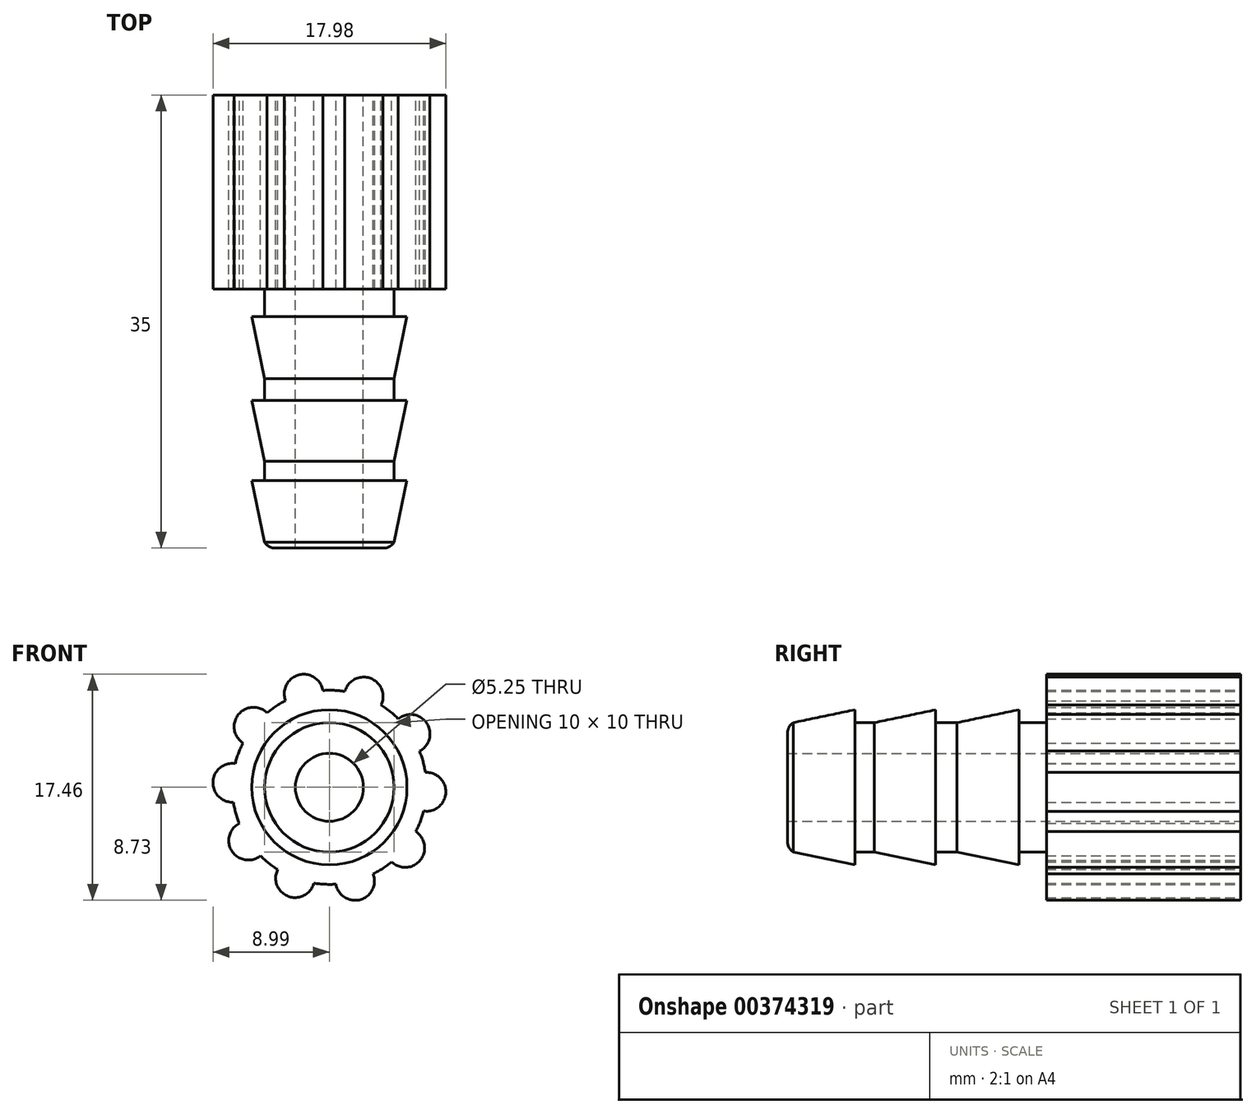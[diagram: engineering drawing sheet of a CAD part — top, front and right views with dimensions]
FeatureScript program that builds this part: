
annotation { "Feature Type Name" : "Feature", "Feature Type Description" : "" }
export const myFeature = defineFeature(function(context is Context, id is Id, definition is map)
    precondition{}
    {
        {
            var Q0;
            Q0=qCreatedBy(makeId("Front.planeOp"),FACE);
            var sketch = newSketch(context, id + "F0", { "sketchPlane" : qUnion([Q0])});
            skArc(sketch, "E0", {"start": v(-3.38, 6.7) * mm, "mid": v(-4.12, 6.27) * mm, "end": v(-4.8, 5.76) * mm});
            skArc(sketch, "E1", {"start": v(3.99, 6.35) * mm, "mid": v(3.18, 8.42) * mm, "end": v(1.2, 7.4) * mm});
            skArc(sketch, "E2.1.0", {"start": v(-0.5, 7.48) * mm, "mid": v(-2.38, 8.68) * mm, "end": v(-3.38, 6.7) * mm});
            skArc(sketch, "E2.2.0", {"start": v(-4.8, 5.76) * mm, "mid": v(-7.03, 5.62) * mm, "end": v(-6.67, 3.43) * mm});
            skArc(sketch, "E2.3.0", {"start": v(-7.27, 1.83) * mm, "mid": v(-9, 0.42) * mm, "end": v(-7.41, -1.15) * mm});
            skArc(sketch, "E2.4.0", {"start": v(-6.96, -2.8) * mm, "mid": v(-7.52, -4.95) * mm, "end": v(-5.32, -5.29) * mm});
            skArc(sketch, "E2.5.0", {"start": v(-3.99, -6.35) * mm, "mid": v(-3.18, -8.42) * mm, "end": v(-1.2, -7.4) * mm});
            skArc(sketch, "E2.6.0", {"start": v(0.5, -7.48) * mm, "mid": v(2.38, -8.68) * mm, "end": v(3.38, -6.7) * mm});
            skArc(sketch, "E2.7.0", {"start": v(4.8, -5.76) * mm, "mid": v(7.03, -5.62) * mm, "end": v(6.67, -3.43) * mm});
            skArc(sketch, "E2.8.0", {"start": v(7.27, -1.83) * mm, "mid": v(9, -0.42) * mm, "end": v(7.41, 1.15) * mm});
            skArc(sketch, "E2.9.0", {"start": v(6.96, 2.8) * mm, "mid": v(7.52, 4.95) * mm, "end": v(5.32, 5.29) * mm});
            skArc(sketch, "E3.trimOffspring", {"start": v(1.2, 7.4) * mm, "mid": v(0.35, 7.5) * mm, "end": v(-0.5, 7.48) * mm});
            skArc(sketch, "E4.trimOffspring", {"start": v(5.32, 5.29) * mm, "mid": v(4.69, 5.86) * mm, "end": v(3.99, 6.35) * mm});
            skArc(sketch, "E5.trimOffspring", {"start": v(7.41, 1.15) * mm, "mid": v(7.23, 1.98) * mm, "end": v(6.96, 2.8) * mm});
            skArc(sketch, "E6.trimOffspring", {"start": v(6.67, -3.43) * mm, "mid": v(7.02, -2.65) * mm, "end": v(7.27, -1.83) * mm});
            skArc(sketch, "E7.trimOffspring", {"start": v(3.38, -6.7) * mm, "mid": v(4.12, -6.27) * mm, "end": v(4.8, -5.76) * mm});
            skArc(sketch, "E8.trimOffspring", {"start": v(-1.2, -7.4) * mm, "mid": v(-0.35, -7.5) * mm, "end": v(0.5, -7.48) * mm});
            skArc(sketch, "E9.trimOffspring", {"start": v(-5.32, -5.29) * mm, "mid": v(-4.69, -5.86) * mm, "end": v(-3.99, -6.35) * mm});
            skArc(sketch, "E10.trimOffspring", {"start": v(-7.41, -1.15) * mm, "mid": v(-7.23, -1.98) * mm, "end": v(-6.96, -2.8) * mm});
            skArc(sketch, "E11.trimOffspring", {"start": v(-6.67, 3.43) * mm, "mid": v(-7.02, 2.65) * mm, "end": v(-7.27, 1.83) * mm});
            skSolve(sketch);
        }
        {
            var Q0;
            Q0=makeQuery(id+"F0.imprint","IMPRINT",FACE,{"disambiguationData":[TD([[makeQuery(id+"F0.imprint","IMPRINT",EDGE,{"derivedFrom":sQuery(id+"F0.wireOp",EDGE,"E0")}),1.0]])]});
            extrude(context, id + "F1", {"entities" : qUnion([Q0]), "depth" : 15 * mm});
        }
        {
            var Q0;
            Q0=makeQuery(id+"F1.opExtrude","CAP_FACE",FACE,{"disambiguationData":[OSD([sQuery(id+"F0.wireOp",EDGE,"E0"),sQuery(id+"F0.wireOp",EDGE,"E1"),sQuery(id+"F0.wireOp",EDGE,"E2.1.0"),sQuery(id+"F0.wireOp",EDGE,"E2.2.0"),sQuery(id+"F0.wireOp",EDGE,"E2.3.0"),sQuery(id+"F0.wireOp",EDGE,"E2.4.0"),sQuery(id+"F0.wireOp",EDGE,"E2.5.0"),sQuery(id+"F0.wireOp",EDGE,"E2.6.0"),sQuery(id+"F0.wireOp",EDGE,"E2.7.0"),sQuery(id+"F0.wireOp",EDGE,"E2.8.0"),sQuery(id+"F0.wireOp",EDGE,"E2.9.0"),sQuery(id+"F0.wireOp",EDGE,"E3.trimOffspring"),sQuery(id+"F0.wireOp",EDGE,"E4.trimOffspring"),sQuery(id+"F0.wireOp",EDGE,"E5.trimOffspring"),sQuery(id+"F0.wireOp",EDGE,"E6.trimOffspring"),sQuery(id+"F0.wireOp",EDGE,"E7.trimOffspring"),sQuery(id+"F0.wireOp",EDGE,"E8.trimOffspring"),sQuery(id+"F0.wireOp",EDGE,"E9.trimOffspring"),sQuery(id+"F0.wireOp",EDGE,"E10.trimOffspring"),sQuery(id+"F0.wireOp",EDGE,"E11.trimOffspring")])],"isStart":true});
            var sketch = newSketch(context, id + "F2", { "sketchPlane" : qUnion([Q0])});
            skCircle(sketch, "E12", {"center": v(0, 0) * mm, "radius": 2.63 * mm});
            skSolve(sketch);
        }
        {
            var Q0;
            Q0=makeQuery(id+"F2.imprint","IMPRINT",FACE,{"disambiguationData":[TD([[makeQuery(id+"F2.imprint","IMPRINT",EDGE,{"derivedFrom":sQuery(id+"F2.wireOp",EDGE,"E12")}),1.0]])]});
            extrude(context, id + "F3", {"entities" : qUnion([Q0]), "operationType" : NewBodyOperationType.REMOVE, "oppositeDirection" : true, "depth" : 12 * mm});
        }
        {
            var Q0;
            Q0=makeQuery(id+"F1.opExtrude","CAP_FACE",FACE,{"disambiguationData":[OSD([sQuery(id+"F0.wireOp",EDGE,"E0"),sQuery(id+"F0.wireOp",EDGE,"E1"),sQuery(id+"F0.wireOp",EDGE,"E2.1.0"),sQuery(id+"F0.wireOp",EDGE,"E2.2.0"),sQuery(id+"F0.wireOp",EDGE,"E2.3.0"),sQuery(id+"F0.wireOp",EDGE,"E2.4.0"),sQuery(id+"F0.wireOp",EDGE,"E2.5.0"),sQuery(id+"F0.wireOp",EDGE,"E2.6.0"),sQuery(id+"F0.wireOp",EDGE,"E2.7.0"),sQuery(id+"F0.wireOp",EDGE,"E2.8.0"),sQuery(id+"F0.wireOp",EDGE,"E2.9.0"),sQuery(id+"F0.wireOp",EDGE,"E3.trimOffspring"),sQuery(id+"F0.wireOp",EDGE,"E4.trimOffspring"),sQuery(id+"F0.wireOp",EDGE,"E5.trimOffspring"),sQuery(id+"F0.wireOp",EDGE,"E6.trimOffspring"),sQuery(id+"F0.wireOp",EDGE,"E7.trimOffspring"),sQuery(id+"F0.wireOp",EDGE,"E8.trimOffspring"),sQuery(id+"F0.wireOp",EDGE,"E9.trimOffspring"),sQuery(id+"F0.wireOp",EDGE,"E10.trimOffspring"),sQuery(id+"F0.wireOp",EDGE,"E11.trimOffspring")])],"isStart":false});
            var sketch = newSketch(context, id + "F4", { "sketchPlane" : qUnion([Q0])});
            skCircle(sketch, "E13", {"center": v(0, 0) * mm, "radius": 5 * mm});
            skSolve(sketch);
        }
        {
            var Q0;
            Q0 = qSketchRegion(id + "F4", true);
            extrude(context, id + "F5", {"entities" : qUnion([Q0]), "operationType" : NewBodyOperationType.ADD, "depth" : 20 * mm});
        }
        {
            var Q0;
            Q0=qCreatedBy(makeId("Right.planeOp"),FACE);
            var sketch = newSketch(context, id + "F6", { "sketchPlane" : qUnion([Q0])});
            skLineSegment(sketch, "E14", {"start": v(-34.99, 4.91) * mm, "end": v(-29.78, 4.91) * mm});
            skLineSegment(sketch, "E15", {"start": v(-29.78, 4.91) * mm, "end": v(-29.78, 6) * mm});
            skLineSegment(sketch, "E16", {"start": v(-29.78, 6) * mm, "end": v(-34.99, 4.91) * mm});
            skLineSegment(sketch, "E17", {"start": v(-28.79, 4.9) * mm, "end": v(-23.58, 4.9) * mm});
            skLineSegment(sketch, "E18", {"start": v(-23.58, 4.9) * mm, "end": v(-23.58, 5.98) * mm});
            skLineSegment(sketch, "E19", {"start": v(-23.58, 5.98) * mm, "end": v(-28.79, 4.9) * mm});
            skLineSegment(sketch, "E20", {"start": v(-22.33, 4.91) * mm, "end": v(-17.12, 4.91) * mm});
            skLineSegment(sketch, "E21", {"start": v(-17.12, 4.91) * mm, "end": v(-17.12, 6) * mm});
            skLineSegment(sketch, "E22", {"start": v(-17.12, 6) * mm, "end": v(-22.33, 4.91) * mm});
            skLineSegment(sketch, "E23", {"start": v(-40.26, 0) * mm, "end": v(-8.8, 0) * mm});
            skSolve(sketch);
        }
        {
            var Q0;
            Q0=makeQuery(id+"F6.imprint","IMPRINT",FACE,{"disambiguationData":[TD([[makeQuery(id+"F6.imprint","IMPRINT",EDGE,{"derivedFrom":sQuery(id+"F6.wireOp",EDGE,"E17")}),1.0]])]});
            var Q1;
            Q1=makeQuery(id+"F6.imprint","IMPRINT",FACE,{"disambiguationData":[TD([[makeQuery(id+"F6.imprint","IMPRINT",EDGE,{"derivedFrom":sQuery(id+"F6.wireOp",EDGE,"E20")}),1.0]])]});
            var Q2;
            Q2=makeQuery(id+"F6.imprint","IMPRINT",FACE,{"disambiguationData":[TD([[makeQuery(id+"F6.imprint","IMPRINT",EDGE,{"derivedFrom":sQuery(id+"F6.wireOp",EDGE,"E14")}),1.0]])]});
            var Q3;
            Q3=sQuery(id+"F6.wireOp",EDGE,"E23");
            revolve(context, id + "F7", {"operationType" : NewBodyOperationType.ADD, "entities" : qUnion([Q0, Q1, Q2]), "axis" : qUnion([Q3]), "revolveType" : RevolveType.FULL});
        }
        {
            var Q0;
            Q0=makeQuery(id+"F5.opExtrude","CAP_EDGE",EDGE,{"disambiguationData":[OSD([sQuery(id+"F4.wireOp",EDGE,"E13")])],"isStart":false});
            fillet(context, id + "F8", {"entities" : qUnion([Q0]), "radius" : 1 * mm, "tangentPropagation" : true, "allowEdgeOverflow" : false});
        }
        {
            var Q0;
            Q0=makeQuery(id+"F5.opExtrude","CAP_FACE",FACE,{"disambiguationData":[OSD([sQuery(id+"F4.wireOp",EDGE,"E13")])],"isStart":false});
            var sketch = newSketch(context, id + "F9", { "sketchPlane" : qUnion([Q0])});
            skCircle(sketch, "E24", {"center": v(0, 0) * mm, "radius": 2.62 * mm});
            skSolve(sketch);
        }
        {
            var Q0;
            Q0 = qSketchRegion(id + "F9", true);
            extrude(context, id + "F10", {"entities" : qUnion([Q0]), "operationType" : NewBodyOperationType.REMOVE, "oppositeDirection" : true, "depth" : 23 * mm});
        }
    });
